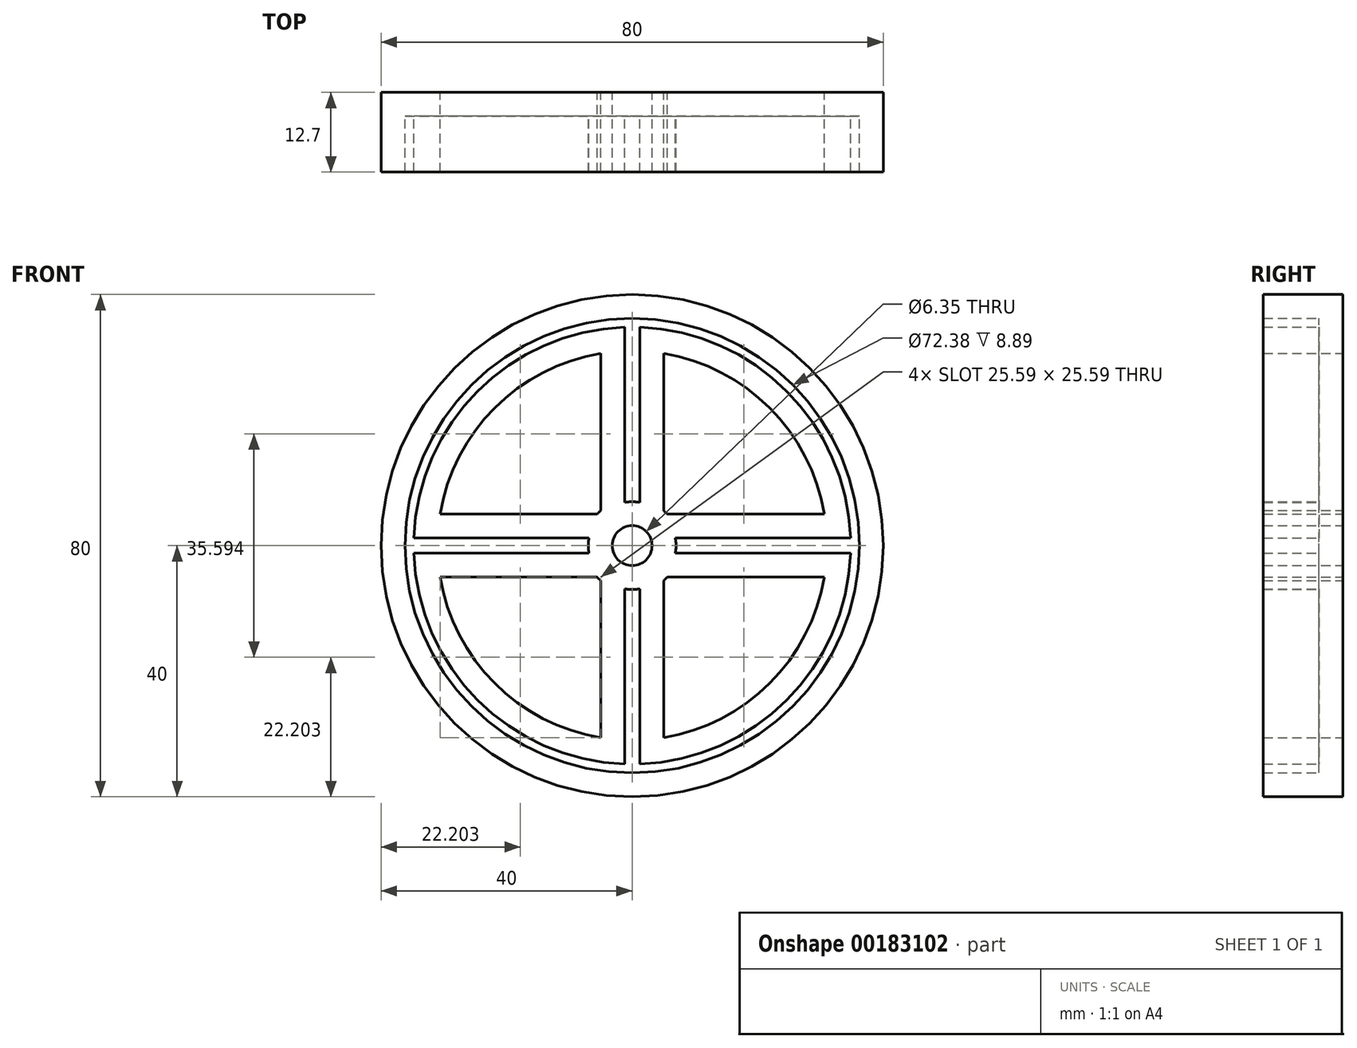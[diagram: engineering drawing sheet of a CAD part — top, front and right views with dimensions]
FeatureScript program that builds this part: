
annotation { "Feature Type Name" : "Feature", "Feature Type Description" : "" }
export const myFeature = defineFeature(function(context is Context, id is Id, definition is map)
    precondition{}
    {
        {
            var Q0;
            Q0=qCreatedBy(makeId("Front.planeOp"),FACE);
            var sketch = newSketch(context, id + "F0", { "sketchPlane" : qUnion([Q0])});
            skCircle(sketch, "E0", {"center": v(0, 0) * mm, "radius": 40 * mm});
            skCircle(sketch, "E1", {"center": v(0, 0) * mm, "radius": 3.18 * mm});
            skLineSegment(sketch, "E2", {"start": v(0, 0) * mm, "end": v(0, 31) * mm, "construction": true});
            skLineSegment(sketch, "E3", {"start": v(0, 0) * mm, "end": v(31, 0) * mm, "construction": true});
            skLineSegment(sketch, "E4", {"start": v(0, 0) * mm, "end": v(0, -31) * mm, "construction": true});
            skLineSegment(sketch, "E5", {"start": v(0, 0) * mm, "end": v(-31, 0) * mm, "construction": true});
            skArc(sketch, "E6", {"start": v(-5, 30.6) * mm, "mid": v(-21.92, 21.92) * mm, "end": v(-30.6, 5) * mm});
            skArc(sketch, "E7", {"start": v(5, -30.6) * mm, "mid": v(21.92, -21.92) * mm, "end": v(30.6, -5) * mm});
            skArc(sketch, "E8.trimOffspring", {"start": v(-30.6, -5) * mm, "mid": v(-21.92, -21.92) * mm, "end": v(-5, -30.6) * mm});
            skArc(sketch, "E9.trimOffspring", {"start": v(30.6, 5) * mm, "mid": v(21.92, 21.92) * mm, "end": v(5, 30.6) * mm});
            skLineSegment(sketch, "E10.trimOffspring", {"start": v(-5.6, 5) * mm, "end": v(-30.6, 5) * mm});
            skLineSegment(sketch, "E11.trimOffspring", {"start": v(-5, 5.6) * mm, "end": v(-5, 5.6) * mm});
            skLineSegment(sketch, "E12.trimOffspring", {"start": v(5.6, 5) * mm, "end": v(5.6, 5) * mm});
            skLineSegment(sketch, "E13.trimOffspring", {"start": v(5, 5.6) * mm, "end": v(5, 30.6) * mm});
            skLineSegment(sketch, "E14.trimOffspring", {"start": v(5.6, -5) * mm, "end": v(30.6, -5) * mm});
            skLineSegment(sketch, "E15.trimOffspring", {"start": v(5, -5.6) * mm, "end": v(5, -30.6) * mm});
            skLineSegment(sketch, "E16.trimOffspring", {"start": v(-5, -5.6) * mm, "end": v(-5, -30.6) * mm});
            skLineSegment(sketch, "E17.trimOffspring", {"start": v(-5.6, -5) * mm, "end": v(-30.6, -5) * mm});
            skArc(sketch, "E18", {"start": v(-5.6, -5) * mm, "mid": v(-5.3, -5.3) * mm, "end": v(-5, -5.6) * mm});
            skArc(sketch, "E19", {"start": v(-5, 5.6) * mm, "mid": v(-5.3, 5.3) * mm, "end": v(-5.6, 5) * mm});
            skArc(sketch, "E20", {"start": v(5.62, 4.97) * mm, "mid": v(5.32, 5.29) * mm, "end": v(5, 5.6) * mm});
            skLineSegment(sketch, "E21", {"start": v(5, -5.6) * mm, "end": v(5, -5.6) * mm});
            skArc(sketch, "E22", {"start": v(5, -5.6) * mm, "mid": v(5.3, -5.3) * mm, "end": v(5.6, -5) * mm});
            skLineSegment(sketch, "E23", {"start": v(5, 5.6) * mm, "end": v(5, 5.6) * mm});
            skLineSegment(sketch, "E24", {"start": v(5.6, 5) * mm, "end": v(30.6, 5) * mm});
            skLineSegment(sketch, "E25", {"start": v(-5, 5.6) * mm, "end": v(-5, 30.6) * mm});
            skLineSegment(sketch, "E26", {"start": v(-5.6, 5) * mm, "end": v(-5.6, 5) * mm});
            skSolve(sketch);
        }
        {
            var Q0;
            Q0=makeQuery(id+"F0.imprint","IMPRINT",FACE,{"disambiguationData":[TD([[makeQuery(id+"F0.imprint","IMPRINT",EDGE,{"derivedFrom":sQuery(id+"F0.wireOp",EDGE,"E0")}),1.0]])]});
            extrude(context, id + "F1", {"entities" : qUnion([Q0]), "endBound" : BoundingType.SYMMETRIC, "depth" : 12.7 * mm});
        }
        {
            var Q0;
            Q0=makeQuery(id+"F1.opExtrude","CAP_FACE",FACE,{"disambiguationData":[OSD([sQuery(id+"F0.wireOp",EDGE,"E0"),sQuery(id+"F0.wireOp",EDGE,"E1"),sQuery(id+"F0.wireOp",EDGE,"E6"),sQuery(id+"F0.wireOp",EDGE,"E7"),sQuery(id+"F0.wireOp",EDGE,"E8.trimOffspring"),sQuery(id+"F0.wireOp",EDGE,"E9.trimOffspring"),sQuery(id+"F0.wireOp",EDGE,"E10.trimOffspring"),sQuery(id+"F0.wireOp",EDGE,"E13.trimOffspring"),sQuery(id+"F0.wireOp",EDGE,"E14.trimOffspring"),sQuery(id+"F0.wireOp",EDGE,"E15.trimOffspring"),sQuery(id+"F0.wireOp",EDGE,"E16.trimOffspring"),sQuery(id+"F0.wireOp",EDGE,"E17.trimOffspring"),sQuery(id+"F0.wireOp",EDGE,"E18"),sQuery(id+"F0.wireOp",EDGE,"E19"),sQuery(id+"F0.wireOp",EDGE,"E20"),sQuery(id+"F0.wireOp",EDGE,"E22"),sQuery(id+"F0.wireOp",EDGE,"E24"),sQuery(id+"F0.wireOp",EDGE,"E25")])],"isStart":false});
            shell(context, id + "F2", {"entities" : qUnion([Q0]), "thickness" : 3.8 * mm});
        }
    });
